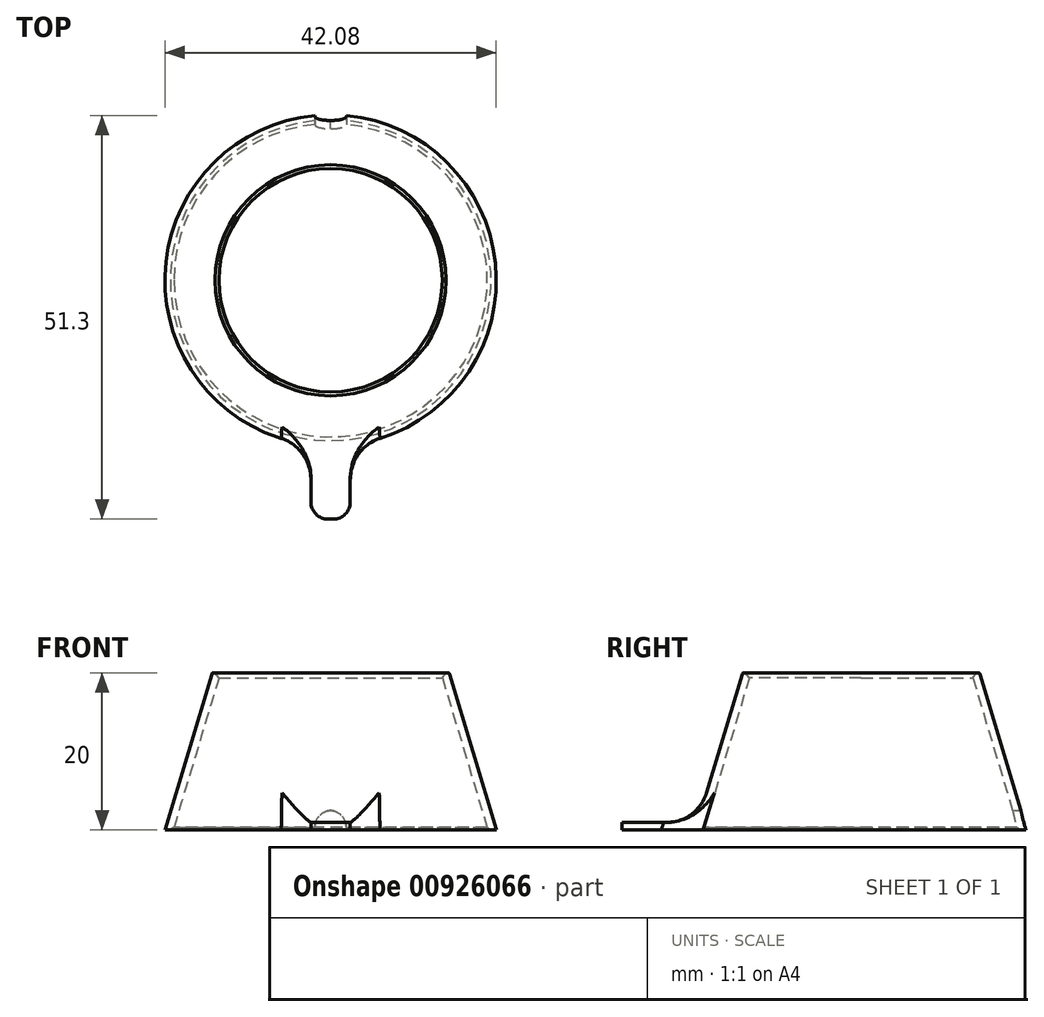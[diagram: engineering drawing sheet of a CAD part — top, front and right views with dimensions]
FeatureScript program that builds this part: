
annotation { "Feature Type Name" : "Feature", "Feature Type Description" : "" }
export const myFeature = defineFeature(function(context is Context, id is Id, definition is map)
    precondition{}
    {
        {
            var Q0;
            Q0=qCreatedBy(makeId("Front.planeOp"),FACE);
            var sketch = newSketch(context, id + "F0", { "sketchPlane" : qUnion([Q0])});
            skLineSegment(sketch, "E0", {"start": v(0, 0) * mm, "end": v(14, 0) * mm});
            skLineSegment(sketch, "E1", {"start": v(0, 0) * mm, "end": v(0, -20) * mm});
            skLineSegment(sketch, "E2", {"start": v(0, -20) * mm, "end": v(20, -20) * mm});
            skLineSegment(sketch, "E3", {"start": v(14, 0) * mm, "end": v(20, -20) * mm});
            skLineSegment(sketch, "E4.0", {"start": v(15.04, 0) * mm, "end": v(20.96, -19.71) * mm});
            skLineSegment(sketch, "E5", {"start": v(14, 0) * mm, "end": v(15.04, 0) * mm});
            skLineSegment(sketch, "E6", {"start": v(20.96, -19.71) * mm, "end": v(21.04, -20) * mm});
            skLineSegment(sketch, "E7", {"start": v(21.04, -20) * mm, "end": v(20, -20) * mm});
            skLineSegment(sketch, "E8", {"start": v(21.04, -20) * mm, "end": v(31.04, -20) * mm});
            skLineSegment(sketch, "E9", {"start": v(31.04, -20) * mm, "end": v(31.04, -19) * mm});
            skLineSegment(sketch, "E10", {"start": v(31.04, -19) * mm, "end": v(20.74, -19) * mm});
            skSolve(sketch);
        }
        {
            var Q0;
            Q0=makeQuery(id+"F0.imprint","IMPRINT",FACE,{"disambiguationData":[TD([[makeQuery(id+"F0.imprint","IMPRINT",EDGE,{"derivedFrom":sQuery(id+"F0.wireOp",EDGE,"E3")}),1.0]])]});
            var Q1;
            Q1=sQuery(id+"F0.wireOp",EDGE,"E1");
            revolve(context, id + "F1", {"surfaceOperationType" : NewSurfaceOperationType.NEW, "entities" : qUnion([Q0]), "axis" : qUnion([Q1]), "revolveType" : RevolveType.FULL});
        }
        {
            var Q0;
            Q0=qCreatedBy(makeId("Top.planeOp"),FACE);
            var sketch = newSketch(context, id + "F2", { "sketchPlane" : qUnion([Q0])});
            skCircle(sketch, "E11", {"center": v(0, 0) * mm, "radius": 20.5 * mm});
            skLineSegment(sketch, "E12", {"start": v(0, 0) * mm, "end": v(2.5, 0) * mm});
            skLineSegment(sketch, "E13", {"start": v(0, 0) * mm, "end": v(-2.5, 0) * mm});
            skLineSegment(sketch, "E14", {"start": v(-2.5, 0) * mm, "end": v(-2.5, -20.35) * mm});
            skLineSegment(sketch, "E15", {"start": v(-2.5, -20.35) * mm, "end": v(-2.5, -30.35) * mm});
            skLineSegment(sketch, "E16", {"start": v(-2.5, -30.35) * mm, "end": v(2.5, -30.35) * mm});
            skLineSegment(sketch, "E17", {"start": v(2.5, -30.35) * mm, "end": v(2.5, -20.35) * mm});
            skLineSegment(sketch, "E18", {"start": v(2.5, -20.35) * mm, "end": v(2.5, 0) * mm});
            skSolve(sketch);
        }
        {
            var Q0;
            {var subQ0=sQuery(id+"F2.wireOp",EDGE,"E15");Q0=makeQuery(id+"F2.imprint","IMPRINT",FACE,{"disambiguationData":[TD([[makeQuery(id+"F2.imprint","IMPRINT",EDGE,{"derivedFrom":subQ0}),1.0]])]});}
            extrude(context, id + "F3", {"entities" : qUnion([Q0]), "operationType" : NewBodyOperationType.ADD, "oppositeDirection" : true, "depth" : 20 * mm, "offsetDistance" : 25 * mm, "hasSecondDirection" : true, "secondDirectionOppositeDirection" : false, "secondDirectionDepth" : -19 * mm});
        }
        {
            var Q0;
            Q0=makeQuery(id+"F3.boolean.opBoolean","INTERSECT",EDGE,{"derivedFrom":[makeQuery(id+"F1.opRevolve","SWEPT_FACE",FACE,{"disambiguationData":[OSD([sQuery(id+"F0.wireOp",EDGE,"E4.0"),sQuery(id+"F0.wireOp",EDGE,"E6")])]}),makeQuery(id+"F3.opExtrude","SWEPT_FACE",FACE,{"disambiguationData":[OSD([sQuery(id+"F2.wireOp",EDGE,"E17")])]})]});
            var Q1;
            Q1=makeQuery(id+"F3.boolean.opBoolean","INTERSECT",EDGE,{"derivedFrom":[makeQuery(id+"F1.opRevolve","SWEPT_FACE",FACE,{"disambiguationData":[OSD([sQuery(id+"F0.wireOp",EDGE,"E4.0"),sQuery(id+"F0.wireOp",EDGE,"E6")])]}),makeQuery(id+"F3.opExtrude","SWEPT_FACE",FACE,{"disambiguationData":[OSD([sQuery(id+"F2.wireOp",EDGE,"E15")])]})]});
            var Q2;
            Q2=makeQuery(id+"F3.boolean.opBoolean","INTERSECT",EDGE,{"derivedFrom":[makeQuery(id+"F1.opRevolve","SWEPT_FACE",FACE,{"disambiguationData":[OSD([sQuery(id+"F0.wireOp",EDGE,"E4.0"),sQuery(id+"F0.wireOp",EDGE,"E6")])]}),makeQuery(id+"F3.opExtrude","CAP_FACE",FACE,{"disambiguationData":[OSD([sQuery(id+"F2.wireOp",EDGE,"E11"),sQuery(id+"F2.wireOp",EDGE,"E15"),sQuery(id+"F2.wireOp",EDGE,"E16"),sQuery(id+"F2.wireOp",EDGE,"E17")])],"isStart":true})]});
            fillet(context, id + "F4", {"entities" : qUnion([Q0, Q1, Q2]), "radius" : 5.28 * mm, "tangentPropagation" : true, "allowEdgeOverflow" : false});
        }
        {
            var Q0;
            Q0=makeQuery(id+"F3.opExtrude","SWEPT_EDGE",EDGE,{"disambiguationData":[OSD([sQuery(id+"F2.wireOp",EDGE,"E16"),sQuery(id+"F2.wireOp",EDGE,"E17")])]});
            var Q1;
            Q1=makeQuery(id+"F3.opExtrude","SWEPT_EDGE",EDGE,{"disambiguationData":[OSD([sQuery(id+"F2.wireOp",EDGE,"E15"),sQuery(id+"F2.wireOp",EDGE,"E16")])]});
            fillet(context, id + "F5", {"entities" : qUnion([Q0, Q1]), "radius" : 2.17 * mm, "tangentPropagation" : true, "allowEdgeOverflow" : false});
        }
        {
            var Q0;
            Q0=makeQuery(id+"F1.opRevolve","SWEPT_EDGE",EDGE,{"disambiguationData":[OSD([sQuery(id+"F0.wireOp",EDGE,"E4.0"),sQuery(id+"F0.wireOp",EDGE,"E5")])]});
            fillet(context, id + "F6", {"entities" : qUnion([Q0]), "radius" : .2 * mm, "tangentPropagation" : true, "allowEdgeOverflow" : false});
        }
        {
            var Q0;
            Q0=qCreatedBy(makeId("Front.planeOp"),FACE);
            var sketch = newSketch(context, id + "F7", { "sketchPlane" : qUnion([Q0])});
            skLineSegment(sketch, "E19", {"start": v(0, 0) * mm, "end": v(0, -20) * mm});
            skLineSegment(sketch, "E20.bottom", {"start": v(-2, -17.5) * mm, "end": v(2, -17.5) * mm});
            skLineSegment(sketch, "E20.top", {"start": v(-2, -22.5) * mm, "end": v(2, -22.5) * mm});
            skLineSegment(sketch, "E20.left", {"start": v(-2, -17.5) * mm, "end": v(-2, -22.5) * mm});
            skLineSegment(sketch, "E20.right", {"start": v(2, -17.5) * mm, "end": v(2, -22.5) * mm});
            skPoint(sketch, "E20.middle", {"position": v(0, -20) * mm});
            skSolve(sketch);
        }
        {
            var Q0;
            Q0 = qSketchRegion(id + "F7", true);
            extrude(context, id + "F8", {"entities" : qUnion([Q0]), "operationType" : NewBodyOperationType.REMOVE, "oppositeDirection" : true, "depth" : 40.7 * mm, "offsetDistance" : 25 * mm});
        }
        {
            var Q0;
            Q0=makeQuery(id+"F8.boolean.opBoolean","COPY",EDGE,{"derivedFrom":makeQuery(id+"F8.opExtrude","SWEPT_EDGE",EDGE,{"disambiguationData":[OSD([sQuery(id+"F7.wireOp",EDGE,"E20.bottom"),sQuery(id+"F7.wireOp",EDGE,"E20.right")])]})});
            var Q1;
            Q1=makeQuery(id+"F8.boolean.opBoolean","COPY",EDGE,{"derivedFrom":makeQuery(id+"F8.opExtrude","SWEPT_EDGE",EDGE,{"disambiguationData":[OSD([sQuery(id+"F7.wireOp",EDGE,"E20.bottom"),sQuery(id+"F7.wireOp",EDGE,"E20.left")])]})});
            fillet(context, id + "F9", {"entities" : qUnion([Q0, Q1]), "radius" : 2.15 * mm, "tangentPropagation" : true, "allowEdgeOverflow" : false});
        }
        {
            var Q0;
            Q0=makeQuery(id+"F1.opRevolve","SWEPT_EDGE",EDGE,{"disambiguationData":[OSD([sQuery(id+"F0.wireOp",EDGE,"E0"),sQuery(id+"F0.wireOp",EDGE,"E3"),sQuery(id+"F0.wireOp",EDGE,"E5")])]});
            var Q1;
            Q1=makeQuery(id+"F1.opRevolve","SWEPT_EDGE",EDGE,{"disambiguationData":[OSD([sQuery(id+"F0.wireOp",EDGE,"E2"),sQuery(id+"F0.wireOp",EDGE,"E3"),sQuery(id+"F0.wireOp",EDGE,"E7")])]});
            chamfer(context, id + "F10", {"entities" : qUnion([Q0, Q1]), "width" : .5 * mm, "tangentPropagation" : true});
        }
    });
